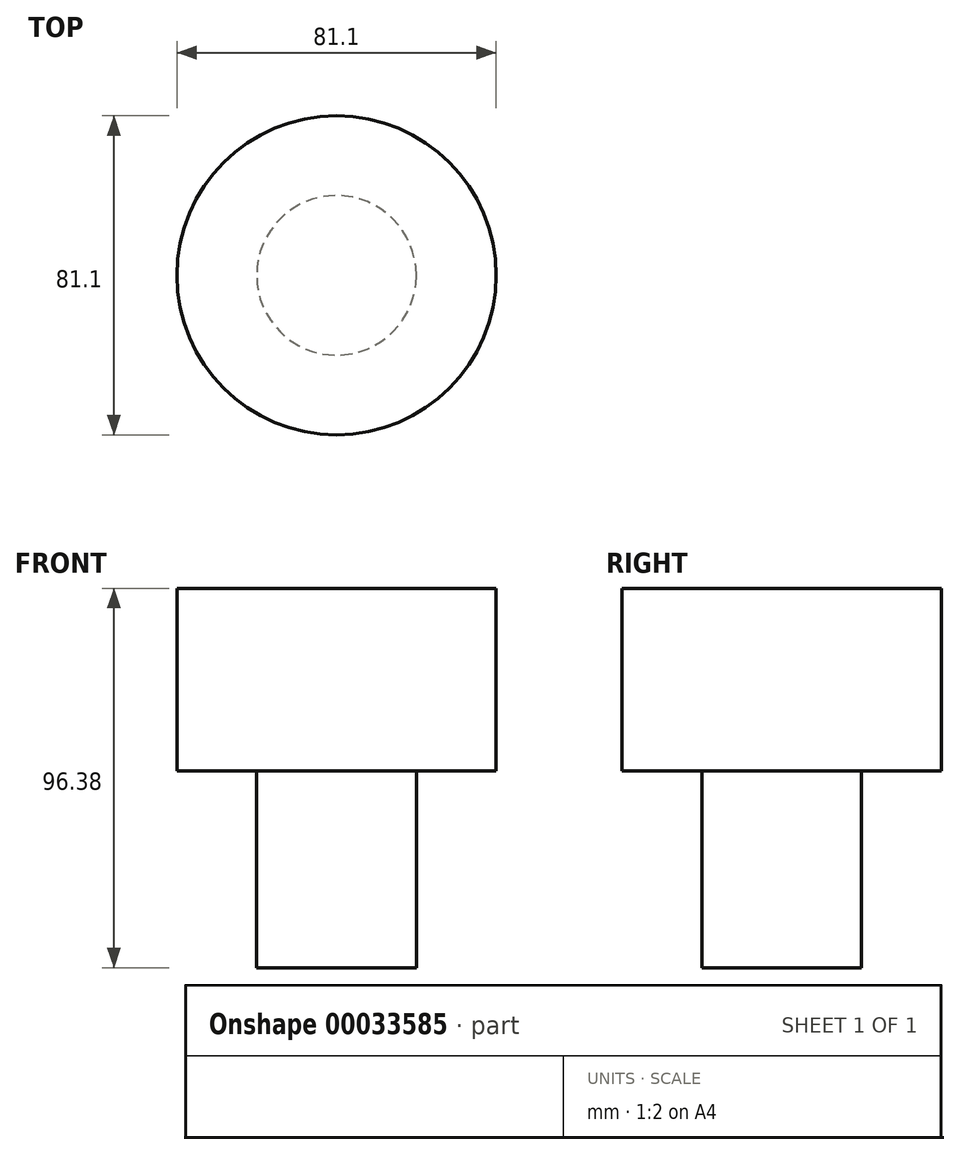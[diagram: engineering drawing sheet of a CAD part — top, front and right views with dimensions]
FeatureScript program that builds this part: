
annotation { "Feature Type Name" : "Feature", "Feature Type Description" : "" }
export const myFeature = defineFeature(function(context is Context, id is Id, definition is map)
    precondition{}
    {
        {
            var Q0;
            Q0=qCreatedBy(makeId("Front.planeOp"),FACE);
            var sketch = newSketch(context, id + "F0", { "sketchPlane" : qUnion([Q0])});
            skLineSegment(sketch, "E0", {"start": v(0, 46.32) * mm, "end": v(-40.55, 46.32) * mm});
            skLineSegment(sketch, "E1", {"start": v(-40.55, 46.32) * mm, "end": v(-40.55, 0) * mm});
            skLineSegment(sketch, "E2", {"start": v(-40.55, 0) * mm, "end": v(-20.28, 0) * mm});
            skLineSegment(sketch, "E3", {"start": v(-20.28, 0) * mm, "end": v(-20.28, -50.06) * mm});
            skLineSegment(sketch, "E4", {"start": v(-20.28, -50.06) * mm, "end": v(0, -50.06) * mm});
            skLineSegment(sketch, "E5", {"start": v(0, -50.06) * mm, "end": v(0, 46.32) * mm});
            skSolve(sketch);
        }
        {
            var Q0;
            Q0=makeQuery(id+"F0.imprint","IMPRINT",FACE,{"disambiguationData":[TD([[makeQuery(id+"F0.imprint","IMPRINT",EDGE,{"derivedFrom":sQuery(id+"F0.wireOp",EDGE,"E0")}),1.0]])]});
            var Q1;
            Q1=sQuery(id+"F0.wireOp",EDGE,"E5");
            revolve(context, id + "F1", {"entities" : qUnion([Q0]), "axis" : qUnion([Q1]), "revolveType" : RevolveType.FULL});
        }
    });
